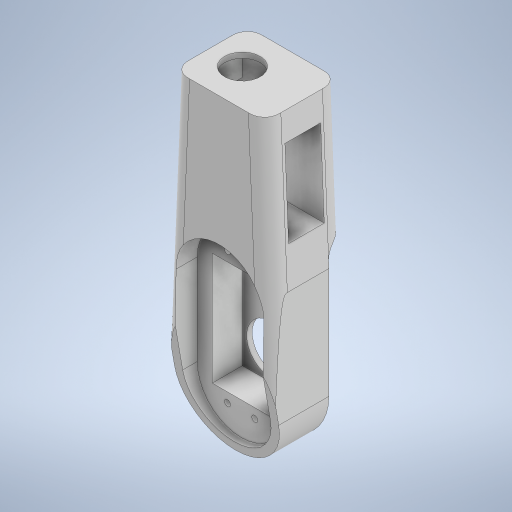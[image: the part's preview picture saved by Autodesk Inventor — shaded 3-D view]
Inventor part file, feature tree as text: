
AUTODESK INVENTOR PART (.ipt)
format: ipt  version: 2024.1 (Build 281209000, 209)  size: 479,232 bytes
history: native  units: in
note: dims shown in document units (in); Inventor stores cm internally (conversion verified against a paired STEP export)
features: extrude x10, sketch x10, fillet x2, direct_edit x1, other x1
ambient origin geometry x8: Origin, YZ Plane, XZ Plane, XY Plane, X Axis, Y Axis, Z Axis, Center Point
bodies: Solid1 (feature_tree)
feature tree (24):
  extrude  "Extrusion1"  Depth=55.5669in
  extrude  "Extrusion2"  Depth=18.9961in
  fillet  "Fillet1"  Radius=40.3543in
  fillet  "Face Fillet1"
  extrude  "Extrusion3"  Depth=18.0004in
  extrude  "Extrusion4"  Depth=21.063in TaperAngle=0.0deg
  extrude  "Extrusion5"  Depth=5.9055in TaperAngle=0.0deg
  extrude  "Extrusion6"  Depth=5.9055in
  extrude  "Extrusion7"  Depth=13.0in
  extrude  "Extrusion8"  Depth=7.0in
  extrude  "Extrusion9"  TaperAngle=90.0deg  [1 undecoded]
  extrude  "Extrusion10"  Depth=0.3937in
  direct_edit  "Direct Edit1"
  sketch  "Sketch1"  dims[d0=33.2677in d1=55.5669in]
  sketch  "Sketch2"  dims[d2=18.9961in d3=18.9961in d4=40.3543in]
  sketch  "Sketch3"  dims[d5=40.3543in d6=18.0004in]
  sketch  "Sketch4"  dims[d7=25.1969in d8=21.063in d9=0.0in]
  sketch  "Sketch5"  dims[d10=47.0in d11=5.9055in d12=0.0in]
  sketch  "Sketch6"  dims[d13=5.9055in d14=5.9055in]
  sketch  "Sketch7"  dims[d15=31.0in d16=13.0in]
  sketch  "Sketch8"  dims[d17=10.0in d18=7.0in]
  sketch  "Sketch9"  dims[d19=37.8145in d20=0.0in d24=90.0deg]
  sketch  "Sketch10"  dims[d25=20.0in d26=7.0in d27=23.0315in d28=13.0in d29=8.0in d30=0.0in d31=13.0in d32=13.5in d33=11.6984in d34=0.0in d35=0.0in d36=2.2047in d37=2.2047in d38=8.0in d39=0.0in d40=71.0in d42=3.0in d43=8.063in d44=0.0in d45=41.0in d46=21.0in d47=8.5in d48=14.9225in d49=11.0in d50=0.0in d51=3.5in d52=3.5in d53=2.2047in d54=2.2047in d55=2.2047in d56=2.2047in d57=4.9606in d58=4.9606in d59=4.9606in d60=4.9606in d61=9.0in d62=0.0in d63=8.0in d64=1.9346in d65=34.8425in d66=0.0in d67=0.0in d68=0.0394in d69=0.3937in d70=0.3937in]
  other  "Scale1"
note: 1 required parameter value undecoded (feature->parameter linkage not recoverable at this tier; creation-order binding heuristic only, values carry confidence <= 0.55)
